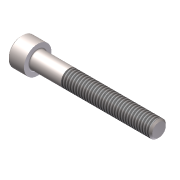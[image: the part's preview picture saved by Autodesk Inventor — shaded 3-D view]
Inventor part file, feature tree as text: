
AUTODESK INVENTOR PART (.ipt)
format: ipt  version: 2011 (Build 150239000, 239)  size: 104,960 bytes
history: native  units: in
note: dims shown in document units (in); Inventor stores cm internally (conversion verified against a paired STEP export)
features: other x1, imported_body x1, thread x1
ambient origin geometry x8: Origin, YZ Plane, XZ Plane, XY Plane, X Axis, Y Axis, Z Axis, Center Point
feature tree (3):
  other  "Hex"
  imported_body  "Base1"
  thread  "Thread1"  [1 undecoded]
note: 1 required parameter value undecoded (feature->parameter linkage not recoverable at this tier; creation-order binding heuristic only, values carry confidence <= 0.55)
